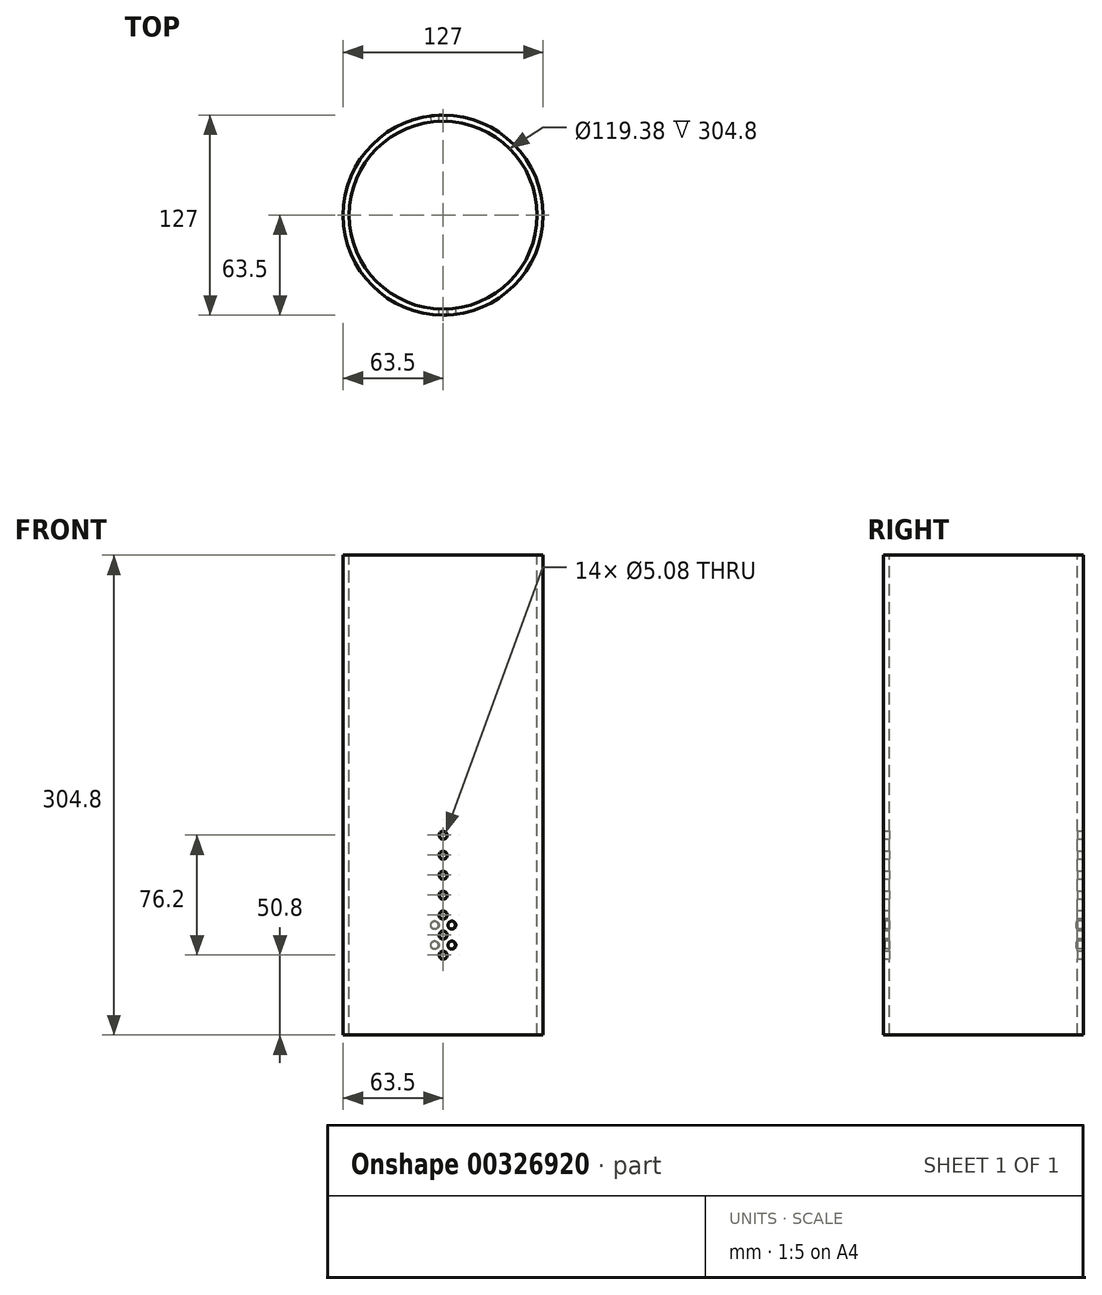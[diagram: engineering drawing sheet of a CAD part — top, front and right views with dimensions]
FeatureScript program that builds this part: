
annotation { "Feature Type Name" : "Feature", "Feature Type Description" : "" }
export const myFeature = defineFeature(function(context is Context, id is Id, definition is map)
    precondition{}
    {
        {
            var Q0;
            Q0=qCreatedBy(makeId("Front.planeOp"),FACE);
            var sketch = newSketch(context, id + "F0", { "sketchPlane" : qUnion([Q0])});
            skLineSegment(sketch, "E0", {"start": v(0, -76.32) * mm, "end": v(0, 76.14) * mm});
            skSolve(sketch);
        }
        {
            var Q0;
            Q0=qCreatedBy(makeId("Front.planeOp"),FACE);
            var Q1;
            Q1=sQuery(id+"F0.wireOp",EDGE,"E0");
            cPlane(context, id + "F1", {"entities" : qUnion([Q0, Q1]), "cplaneType" : CPlaneType.LINE_ANGLE, "offset" : 25.4 * mm, "angle" : 0 * degree, "width" : 152.4 * mm, "height" : 152.4 * mm});
        }
        {
            var Q0;
            Q0=qCreatedBy(id+"F1.planeOp",FACE);
            var Q1;
            Q1=sQuery(id+"F0.wireOp",EDGE,"E0");
            cPlane(context, id + "F2", {"entities" : qUnion([Q0, Q1]), "cplaneType" : CPlaneType.LINE_ANGLE, "offset" : 25.4 * mm, "angle" : 5 * degree, "width" : 152.4 * mm, "height" : 152.4 * mm});
        }
        {
            var Q0;
            Q0=qCreatedBy(id+"F1.planeOp",FACE);
            var Q1;
            Q1 = qBodyType(qCreatedBy(id + "F0" ,EDGE), BodyType.WIRE);
            cPlane(context, id + "F3", {"entities" : qUnion([Q0, Q1]), "cplaneType" : CPlaneType.LINE_ANGLE, "offset" : 25.4 * mm, "angle" : 15 * degree, "width" : 152.4 * mm, "height" : 152.4 * mm});
        }
        {
            var Q0;
            Q0=qCreatedBy(id+"F3.planeOp",FACE);
            var Q1;
            Q1 = qBodyType(qCreatedBy(id + "F0" ,EDGE), BodyType.WIRE);
            cPlane(context, id + "F4", {"entities" : qUnion([Q0, Q1]), "cplaneType" : CPlaneType.LINE_ANGLE, "offset" : 25.4 * mm, "angle" : 5 * degree, "width" : 152.4 * mm, "height" : 152.4 * mm});
        }
        {
            var Q0;
            Q0=qCreatedBy(id+"F4.planeOp",FACE);
            var Q1;
            Q1 = qBodyType(qCreatedBy(id + "F0" ,EDGE), BodyType.WIRE);
            cPlane(context, id + "F5", {"entities" : qUnion([Q0, Q1]), "cplaneType" : CPlaneType.LINE_ANGLE, "offset" : 25.4 * mm, "angle" : 5 * degree, "width" : 152.4 * mm, "height" : 152.4 * mm});
        }
        {
            var Q0;
            Q0=qCreatedBy(id+"F5.planeOp",FACE);
            var Q1;
            Q1 = qBodyType(qCreatedBy(id + "F0" ,EDGE), BodyType.WIRE);
            cPlane(context, id + "F6", {"entities" : qUnion([Q0, Q1]), "cplaneType" : CPlaneType.LINE_ANGLE, "offset" : 25.4 * mm, "angle" : 5 * degree, "width" : 152.4 * mm, "height" : 152.4 * mm});
        }
        {
            var Q0;
            Q0=qCreatedBy(id+"F6.planeOp",FACE);
            var Q1;
            Q1 = qBodyType(qCreatedBy(id + "F0" ,EDGE), BodyType.WIRE);
            cPlane(context, id + "F7", {"entities" : qUnion([Q0, Q1]), "cplaneType" : CPlaneType.LINE_ANGLE, "offset" : 25.4 * mm, "angle" : 5 * degree, "width" : 152.4 * mm, "height" : 152.4 * mm});
        }
        {
            var Q0;
            Q0=qCreatedBy(id+"F7.planeOp",FACE);
            var Q1;
            Q1 = qBodyType(qCreatedBy(id + "F0" ,EDGE), BodyType.WIRE);
            cPlane(context, id + "F8", {"entities" : qUnion([Q0, Q1]), "cplaneType" : CPlaneType.LINE_ANGLE, "offset" : 25.4 * mm, "angle" : 5 * degree, "width" : 152.4 * mm, "height" : 152.4 * mm});
        }
        {
            var Q0;
            Q0=qCreatedBy(id+"F8.planeOp",FACE);
            var Q1;
            Q1 = qBodyType(qCreatedBy(id + "F0" ,EDGE), BodyType.WIRE);
            cPlane(context, id + "F9", {"entities" : qUnion([Q0, Q1]), "cplaneType" : CPlaneType.LINE_ANGLE, "offset" : 25.4 * mm, "angle" : 5 * degree, "width" : 152.4 * mm, "height" : 152.4 * mm});
        }
        {
            var Q0;
            Q0=qCreatedBy(id+"F9.planeOp",FACE);
            var Q1;
            Q1 = qBodyType(qCreatedBy(id + "F0" ,EDGE), BodyType.WIRE);
            cPlane(context, id + "F10", {"entities" : qUnion([Q0, Q1]), "cplaneType" : CPlaneType.LINE_ANGLE, "offset" : 25.4 * mm, "angle" : 5 * degree, "width" : 152.4 * mm, "height" : 152.4 * mm});
        }
        {
            var Q0;
            Q0=qCreatedBy(id+"F10.planeOp",FACE);
            var Q1;
            Q1 = qBodyType(qCreatedBy(id + "F0" ,EDGE), BodyType.WIRE);
            cPlane(context, id + "F11", {"entities" : qUnion([Q0, Q1]), "cplaneType" : CPlaneType.LINE_ANGLE, "offset" : 25.4 * mm, "angle" : 5 * degree, "width" : 152.4 * mm, "height" : 152.4 * mm});
        }
        {
            var Q0;
            Q0=qCreatedBy(id+"F11.planeOp",FACE);
            var Q1;
            Q1 = qBodyType(qCreatedBy(id + "F0" ,EDGE), BodyType.WIRE);
            cPlane(context, id + "F12", {"entities" : qUnion([Q0, Q1]), "cplaneType" : CPlaneType.LINE_ANGLE, "offset" : 25.4 * mm, "angle" : 5 * degree, "width" : 152.4 * mm, "height" : 152.4 * mm});
        }
        {
            var Q0;
            Q0=qCreatedBy(id+"F12.planeOp",FACE);
            var Q1;
            Q1 = qBodyType(qCreatedBy(id + "F0" ,EDGE), BodyType.WIRE);
            cPlane(context, id + "F13", {"entities" : qUnion([Q0, Q1]), "cplaneType" : CPlaneType.LINE_ANGLE, "offset" : 25.4 * mm, "angle" : 5 * degree, "width" : 152.4 * mm, "height" : 152.4 * mm});
        }
        {
            var Q0;
            Q0=qCreatedBy(id+"F13.planeOp",FACE);
            var Q1;
            Q1 = qBodyType(qCreatedBy(id + "F0" ,EDGE), BodyType.WIRE);
            cPlane(context, id + "F14", {"entities" : qUnion([Q0, Q1]), "cplaneType" : CPlaneType.LINE_ANGLE, "offset" : 25.4 * mm, "angle" : 5 * degree, "width" : 152.4 * mm, "height" : 152.4 * mm});
        }
        {
            var Q0;
            Q0=qCreatedBy(id+"F14.planeOp",FACE);
            var Q1;
            Q1 = qBodyType(qCreatedBy(id + "F0" ,EDGE), BodyType.WIRE);
            cPlane(context, id + "F15", {"entities" : qUnion([Q0, Q1]), "cplaneType" : CPlaneType.LINE_ANGLE, "offset" : 25.4 * mm, "angle" : 5 * degree, "width" : 152.4 * mm, "height" : 152.4 * mm});
        }
        {
            var Q0;
            Q0=qCreatedBy(id+"F15.planeOp",FACE);
            var Q1;
            Q1 = qBodyType(qCreatedBy(id + "F0" ,EDGE), BodyType.WIRE);
            cPlane(context, id + "F16", {"entities" : qUnion([Q0, Q1]), "cplaneType" : CPlaneType.LINE_ANGLE, "offset" : 25.4 * mm, "angle" : 5 * degree, "width" : 152.4 * mm, "height" : 152.4 * mm});
        }
        {
            var Q0;
            Q0=qCreatedBy(id+"F16.planeOp",FACE);
            var Q1;
            Q1 = qBodyType(qCreatedBy(id + "F0" ,EDGE), BodyType.WIRE);
            cPlane(context, id + "F17", {"entities" : qUnion([Q0, Q1]), "cplaneType" : CPlaneType.LINE_ANGLE, "offset" : 25.4 * mm, "angle" : 5 * degree, "width" : 152.4 * mm, "height" : 152.4 * mm});
        }
        {
            var Q0;
            Q0=qCreatedBy(id+"F17.planeOp",FACE);
            var Q1;
            Q1 = qBodyType(qCreatedBy(id + "F0" ,EDGE), BodyType.WIRE);
            cPlane(context, id + "F18", {"entities" : qUnion([Q0, Q1]), "cplaneType" : CPlaneType.LINE_ANGLE, "offset" : 25.4 * mm, "angle" : 5 * degree, "width" : 152.4 * mm, "height" : 152.4 * mm});
        }
        {
            var Q0;
            Q0=qCreatedBy(id+"F18.planeOp",FACE);
            var Q1;
            Q1 = qBodyType(qCreatedBy(id + "F0" ,EDGE), BodyType.WIRE);
            cPlane(context, id + "F19", {"entities" : qUnion([Q0, Q1]), "cplaneType" : CPlaneType.LINE_ANGLE, "offset" : 25.4 * mm, "angle" : 5 * degree, "width" : 152.4 * mm, "height" : 152.4 * mm});
        }
        {
            var Q0;
            Q0=qCreatedBy(id+"F19.planeOp",FACE);
            var Q1;
            Q1 = qBodyType(qCreatedBy(id + "F0" ,EDGE), BodyType.WIRE);
            cPlane(context, id + "F20", {"entities" : qUnion([Q0, Q1]), "cplaneType" : CPlaneType.LINE_ANGLE, "offset" : 25.4 * mm, "angle" : 5 * degree, "width" : 152.4 * mm, "height" : 152.4 * mm});
        }
        {
            var Q0;
            Q0=qCreatedBy(id+"F20.planeOp",FACE);
            var Q1;
            Q1 = qBodyType(qCreatedBy(id + "F0" ,EDGE), BodyType.WIRE);
            cPlane(context, id + "F21", {"entities" : qUnion([Q0, Q1]), "cplaneType" : CPlaneType.LINE_ANGLE, "offset" : 25.4 * mm, "angle" : 5 * degree, "width" : 152.4 * mm, "height" : 152.4 * mm});
        }
        {
            var Q0;
            Q0=qCreatedBy(id+"F21.planeOp",FACE);
            var Q1;
            Q1 = qBodyType(qCreatedBy(id + "F0" ,EDGE), BodyType.WIRE);
            cPlane(context, id + "F22", {"entities" : qUnion([Q0, Q1]), "cplaneType" : CPlaneType.LINE_ANGLE, "offset" : 25.4 * mm, "angle" : 5 * degree, "width" : 152.4 * mm, "height" : 152.4 * mm});
        }
        {
            var Q0;
            Q0=qCreatedBy(id+"F22.planeOp",FACE);
            var Q1;
            Q1 = qBodyType(qCreatedBy(id + "F0" ,EDGE), BodyType.WIRE);
            cPlane(context, id + "F23", {"entities" : qUnion([Q0, Q1]), "cplaneType" : CPlaneType.LINE_ANGLE, "offset" : 25.4 * mm, "angle" : 5 * degree, "width" : 152.4 * mm, "height" : 152.4 * mm});
        }
        {
            var Q0;
            Q0=qCreatedBy(id+"F23.planeOp",FACE);
            var Q1;
            Q1 = qBodyType(qCreatedBy(id + "F0" ,EDGE), BodyType.WIRE);
            cPlane(context, id + "F24", {"entities" : qUnion([Q0, Q1]), "cplaneType" : CPlaneType.LINE_ANGLE, "offset" : 25.4 * mm, "angle" : 5 * degree, "width" : 152.4 * mm, "height" : 152.4 * mm});
        }
        {
            var Q0;
            Q0=qCreatedBy(id+"F24.planeOp",FACE);
            var Q1;
            Q1 = qBodyType(qCreatedBy(id + "F0" ,EDGE), BodyType.WIRE);
            cPlane(context, id + "F25", {"entities" : qUnion([Q0, Q1]), "cplaneType" : CPlaneType.LINE_ANGLE, "offset" : 25.4 * mm, "angle" : 5 * degree, "width" : 152.4 * mm, "height" : 152.4 * mm});
        }
        {
            var Q0;
            Q0=qCreatedBy(id+"F25.planeOp",FACE);
            var Q1;
            Q1 = qBodyType(qCreatedBy(id + "F0" ,EDGE), BodyType.WIRE);
            cPlane(context, id + "F26", {"entities" : qUnion([Q0, Q1]), "cplaneType" : CPlaneType.LINE_ANGLE, "offset" : 25.4 * mm, "angle" : 5 * degree, "width" : 152.4 * mm, "height" : 152.4 * mm});
        }
        {
            var Q0;
            Q0=qCreatedBy(id+"F26.planeOp",FACE);
            var Q1;
            Q1 = qBodyType(qCreatedBy(id + "F0" ,EDGE), BodyType.WIRE);
            cPlane(context, id + "F27", {"entities" : qUnion([Q0, Q1]), "cplaneType" : CPlaneType.LINE_ANGLE, "offset" : 25.4 * mm, "angle" : 5 * degree, "width" : 152.4 * mm, "height" : 152.4 * mm});
        }
        {
            var Q0;
            Q0=qCreatedBy(id+"F27.planeOp",FACE);
            var Q1;
            Q1 = qBodyType(qCreatedBy(id + "F0" ,EDGE), BodyType.WIRE);
            cPlane(context, id + "F28", {"entities" : qUnion([Q0, Q1]), "cplaneType" : CPlaneType.LINE_ANGLE, "offset" : 25.4 * mm, "angle" : 5 * degree, "width" : 152.4 * mm, "height" : 152.4 * mm});
        }
        {
            var Q0;
            Q0=qCreatedBy(id+"F28.planeOp",FACE);
            var Q1;
            Q1 = qBodyType(qCreatedBy(id + "F0" ,EDGE), BodyType.WIRE);
            cPlane(context, id + "F29", {"entities" : qUnion([Q0, Q1]), "cplaneType" : CPlaneType.LINE_ANGLE, "offset" : 25.4 * mm, "angle" : 5 * degree, "width" : 152.4 * mm, "height" : 152.4 * mm});
        }
        {
            var Q0;
            Q0=qCreatedBy(id+"F29.planeOp",FACE);
            var Q1;
            Q1 = qBodyType(qCreatedBy(id + "F0" ,EDGE), BodyType.WIRE);
            cPlane(context, id + "F30", {"entities" : qUnion([Q0, Q1]), "cplaneType" : CPlaneType.LINE_ANGLE, "offset" : 25.4 * mm, "angle" : 5 * degree, "width" : 152.4 * mm, "height" : 152.4 * mm});
        }
        {
            var Q0;
            Q0=qCreatedBy(id+"F30.planeOp",FACE);
            var Q1;
            Q1 = qBodyType(qCreatedBy(id + "F0" ,EDGE), BodyType.WIRE);
            cPlane(context, id + "F31", {"entities" : qUnion([Q0, Q1]), "cplaneType" : CPlaneType.LINE_ANGLE, "offset" : 25.4 * mm, "angle" : 5 * degree, "width" : 152.4 * mm, "height" : 152.4 * mm});
        }
        {
            var Q0;
            Q0=qCreatedBy(id+"F31.planeOp",FACE);
            var Q1;
            Q1 = qBodyType(qCreatedBy(id + "F0" ,EDGE), BodyType.WIRE);
            cPlane(context, id + "F32", {"entities" : qUnion([Q0, Q1]), "cplaneType" : CPlaneType.LINE_ANGLE, "offset" : 25.4 * mm, "angle" : 5 * degree, "width" : 152.4 * mm, "height" : 152.4 * mm});
        }
        {
            var Q0;
            Q0=qCreatedBy(id+"F32.planeOp",FACE);
            var Q1;
            Q1 = qBodyType(qCreatedBy(id + "F0" ,EDGE), BodyType.WIRE);
            cPlane(context, id + "F33", {"entities" : qUnion([Q0, Q1]), "cplaneType" : CPlaneType.LINE_ANGLE, "offset" : 25.4 * mm, "angle" : 5 * degree, "width" : 152.4 * mm, "height" : 152.4 * mm});
        }
        {
            var Q0;
            Q0=qCreatedBy(id+"F33.planeOp",FACE);
            var Q1;
            Q1 = qBodyType(qCreatedBy(id + "F0" ,EDGE), BodyType.WIRE);
            cPlane(context, id + "F34", {"entities" : qUnion([Q0, Q1]), "cplaneType" : CPlaneType.LINE_ANGLE, "offset" : 25.4 * mm, "angle" : 5 * degree, "width" : 152.4 * mm, "height" : 152.4 * mm});
        }
        {
            var Q0;
            Q0=qCreatedBy(makeId("Top.planeOp"),FACE);
            var sketch = newSketch(context, id + "F35", { "sketchPlane" : qUnion([Q0])});
            skCircle(sketch, "E1", {"center": v(0, 0) * mm, "radius": 63.5 * mm});
            skSolve(sketch);
        }
        {
            var Q0;
            Q0 = qSketchRegion(id + "F35", true);
            extrude(context, id + "F36", {"entities" : qUnion([Q0]), "depth" : 304.8 * mm});
        }
        {
            var Q0;
            Q0=makeQuery(id+"F36.opExtrude","CAP_FACE",FACE,{"disambiguationData":[OSD([sQuery(id+"F35.wireOp",EDGE,"E1")])],"isStart":false});
            var sketch = newSketch(context, id + "F37", { "sketchPlane" : qUnion([Q0])});
            skPoint(sketch, "E2", {"position": v(0, 0) * mm});
            skSolve(sketch);
        }
        {
            var Q0;
            Q0=makeQuery(id+"F37.imprint","IMPRINT",FACE,{"disambiguationData":[TD([[makeQuery(id+"F37.imprint","IMPRINT",EDGE,{"derivedFrom":makeQuery(id+"F36.opExtrude","CAP_EDGE",EDGE,{"disambiguationData":[OSD([sQuery(id+"F35.wireOp",EDGE,"E1")])],"isStart":false})}),1.0]])]});
            var sketch = newSketch(context, id + "F38", { "sketchPlane" : qUnion([Q0])});
            skCircle(sketch, "E3", {"center": v(0, 0) * mm, "radius": 59.7 * mm});
            skSolve(sketch);
        }
        {
            var Q0;
            Q0 = qSketchRegion(id + "F38", true);
            extrude(context, id + "F39", {"entities" : qUnion([Q0]), "operationType" : NewBodyOperationType.REMOVE, "endBound" : BoundingType.THROUGH_ALL, "oppositeDirection" : true, "depth" : 25.4 * mm});
        }
        {
            var Q0;
            Q0=qCreatedBy(id+"F1.planeOp",FACE);
            var sketch = newSketch(context, id + "F40", { "sketchPlane" : qUnion([Q0])});
            skCircle(sketch, "E4", {"center": v(0, 50.8) * mm, "radius": 2.54 * mm});
            skSolve(sketch);
        }
        {
            var Q0;
            Q0=qCreatedBy(id+"F1.planeOp",FACE);
            var sketch = newSketch(context, id + "F41", { "sketchPlane" : qUnion([Q0])});
            skCircle(sketch, "E5", {"center": v(0, 63.5) * mm, "radius": 2.54 * mm});
            skSolve(sketch);
        }
        {
            var Q0;
            Q0=qCreatedBy(id+"F1.planeOp",FACE);
            var sketch = newSketch(context, id + "F42", { "sketchPlane" : qUnion([Q0])});
            skCircle(sketch, "E6", {"center": v(0, 76.2) * mm, "radius": 2.54 * mm});
            skSolve(sketch);
        }
        {
            var Q0;
            Q0=qCreatedBy(id+"F1.planeOp",FACE);
            var sketch = newSketch(context, id + "F43", { "sketchPlane" : qUnion([Q0])});
            skCircle(sketch, "E7", {"center": v(0, 88.9) * mm, "radius": 2.54 * mm});
            skSolve(sketch);
        }
        {
            var Q0;
            Q0=qCreatedBy(id+"F1.planeOp",FACE);
            var sketch = newSketch(context, id + "F44", { "sketchPlane" : qUnion([Q0])});
            skCircle(sketch, "E8", {"center": v(0, 101.6) * mm, "radius": 2.54 * mm});
            skSolve(sketch);
        }
        {
            var Q0;
            Q0=qCreatedBy(id+"F1.planeOp",FACE);
            var sketch = newSketch(context, id + "F45", { "sketchPlane" : qUnion([Q0])});
            skCircle(sketch, "E9", {"center": v(0, 114.3) * mm, "radius": 2.54 * mm});
            skSolve(sketch);
        }
        {
            var Q0;
            Q0=qCreatedBy(id+"F1.planeOp",FACE);
            var sketch = newSketch(context, id + "F46", { "sketchPlane" : qUnion([Q0])});
            skCircle(sketch, "E10", {"center": v(0, 127) * mm, "radius": 2.54 * mm});
            skSolve(sketch);
        }
        {
            var Q0;
            Q0 = qSketchRegion(id + "F40", true);
            extrude(context, id + "F47", {"entities" : qUnion([Q0]), "operationType" : NewBodyOperationType.REMOVE, "endBound" : BoundingType.SYMMETRIC, "oppositeDirection" : true, "depth" : 127 * mm});
        }
        {
            var Q0;
            Q0 = qSketchRegion(id + "F41", true);
            extrude(context, id + "F48", {"entities" : qUnion([Q0]), "operationType" : NewBodyOperationType.REMOVE, "endBound" : BoundingType.SYMMETRIC, "depth" : 127 * mm});
        }
        {
            var Q0;
            Q0 = qSketchRegion(id + "F42", true);
            extrude(context, id + "F49", {"entities" : qUnion([Q0]), "operationType" : NewBodyOperationType.REMOVE, "endBound" : BoundingType.SYMMETRIC, "depth" : 127 * mm});
        }
        {
            var Q0;
            Q0 = qSketchRegion(id + "F43", true);
            extrude(context, id + "F50", {"entities" : qUnion([Q0]), "operationType" : NewBodyOperationType.REMOVE, "endBound" : BoundingType.SYMMETRIC, "oppositeDirection" : true, "depth" : 127 * mm});
        }
        {
            var Q0;
            Q0 = qSketchRegion(id + "F44", true);
            extrude(context, id + "F51", {"entities" : qUnion([Q0]), "operationType" : NewBodyOperationType.REMOVE, "endBound" : BoundingType.SYMMETRIC, "oppositeDirection" : true, "depth" : 127 * mm});
        }
        {
            var Q0;
            Q0 = qSketchRegion(id + "F45", true);
            extrude(context, id + "F52", {"entities" : qUnion([Q0]), "operationType" : NewBodyOperationType.REMOVE, "endBound" : BoundingType.SYMMETRIC, "oppositeDirection" : true, "depth" : 127 * mm});
        }
        {
            var Q0;
            Q0 = qSketchRegion(id + "F46", true);
            extrude(context, id + "F53", {"entities" : qUnion([Q0]), "operationType" : NewBodyOperationType.REMOVE, "endBound" : BoundingType.SYMMETRIC, "oppositeDirection" : true, "depth" : 127 * mm});
        }
        {
            var Q0;
            Q0=qCreatedBy(id+"F2.planeOp",FACE);
            var sketch = newSketch(context, id + "F54", { "sketchPlane" : qUnion([Q0])});
            skCircle(sketch, "E11", {"center": v(0, 57.15) * mm, "radius": 2.54 * mm});
            skSolve(sketch);
        }
        {
            var Q0;
            Q0=qCreatedBy(id+"F2.planeOp",FACE);
            var sketch = newSketch(context, id + "F55", { "sketchPlane" : qUnion([Q0])});
            skCircle(sketch, "E12", {"center": v(0, 69.85) * mm, "radius": 2.54 * mm});
            skSolve(sketch);
        }
        {
            var Q0;
            Q0=qCreatedBy(id+"F2.planeOp",FACE);
            var sketch = newSketch(context, id + "F56", { "sketchPlane" : qUnion([Q0])});
            skCircle(sketch, "E13", {"center": v(0, 82.55) * mm, "radius": 2.54 * mm});
            skSolve(sketch);
        }
        {
            var Q0;
            Q0=qCreatedBy(id+"F2.planeOp",FACE);
            var sketch = newSketch(context, id + "F57", { "sketchPlane" : qUnion([Q0])});
            skCircle(sketch, "E14", {"center": v(0, 95.25) * mm, "radius": 2.54 * mm});
            skSolve(sketch);
        }
        {
            var Q0;
            Q0=qCreatedBy(id+"F2.planeOp",FACE);
            var sketch = newSketch(context, id + "F58", { "sketchPlane" : qUnion([Q0])});
            skCircle(sketch, "E15", {"center": v(0, 107.95) * mm, "radius": 2.54 * mm});
            skSolve(sketch);
        }
        {
            var Q0;
            Q0 = qSketchRegion(id + "F54", true);
            extrude(context, id + "F59", {"entities" : qUnion([Q0]), "operationType" : NewBodyOperationType.REMOVE, "endBound" : BoundingType.SYMMETRIC, "oppositeDirection" : true, "depth" : 127 * mm});
        }
        {
            var Q0;
            Q0 = qSketchRegion(id + "F55", true);
            extrude(context, id + "F60", {"entities" : qUnion([Q0]), "operationType" : NewBodyOperationType.REMOVE, "endBound" : BoundingType.SYMMETRIC, "oppositeDirection" : true, "depth" : 127 * mm});
        }
    });
